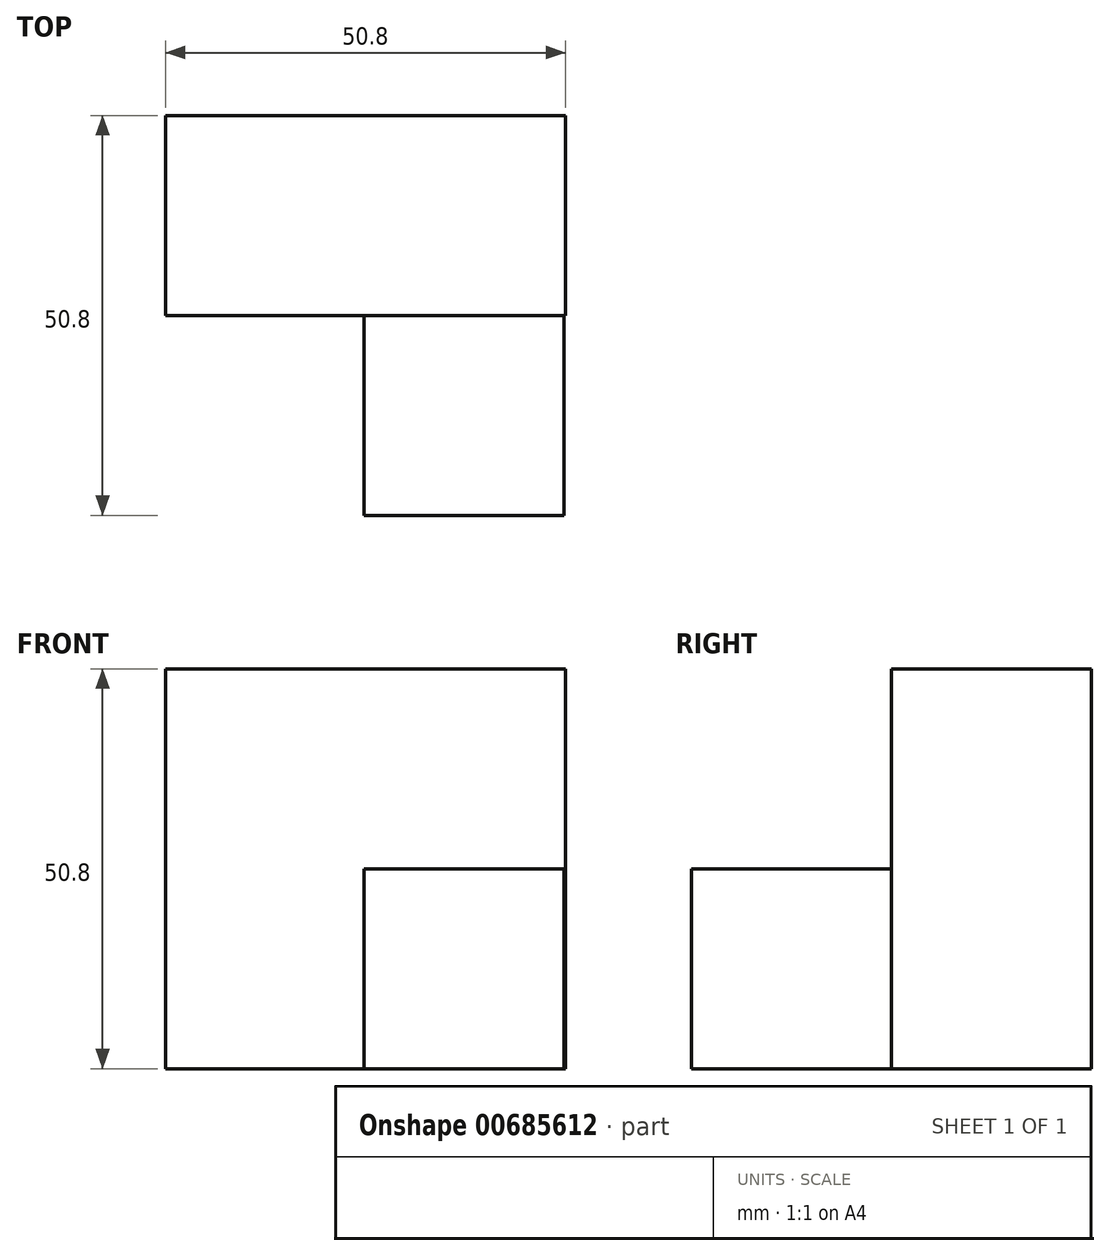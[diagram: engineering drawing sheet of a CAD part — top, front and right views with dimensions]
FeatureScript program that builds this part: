
annotation { "Feature Type Name" : "Feature", "Feature Type Description" : "" }
export const myFeature = defineFeature(function(context is Context, id is Id, definition is map)
    precondition{}
    {
        {
            var Q0;
            Q0=qCreatedBy(makeId("Front.planeOp"),FACE);
            var sketch = newSketch(context, id + "F0", { "sketchPlane" : qUnion([Q0])});
            skLineSegment(sketch, "E0.bottom", {"start": v(-31.04, 53.76) * mm, "end": v(19.76, 53.76) * mm});
            skLineSegment(sketch, "E0.top", {"start": v(-31.04, 2.96) * mm, "end": v(19.76, 2.96) * mm});
            skLineSegment(sketch, "E0.left", {"start": v(-31.04, 53.76) * mm, "end": v(-31.04, 2.96) * mm});
            skLineSegment(sketch, "E0.right", {"start": v(19.76, 53.76) * mm, "end": v(19.76, 2.96) * mm});
            skSolve(sketch);
        }
        {
            var Q0;
            Q0 = qSketchRegion(id + "F0", true);
            extrude(context, id + "F1", {"entities" : qUnion([Q0]), "depth" : 25.4 * mm, "offsetDistance" : 25.4 * mm});
        }
        {
            var Q0;
            Q0=qCreatedBy(makeId("Front.planeOp"),FACE);
            var sketch = newSketch(context, id + "F2", { "sketchPlane" : qUnion([Q0])});
            skLineSegment(sketch, "E1.bottom", {"start": v(19.58, 2.96) * mm, "end": v(-5.82, 2.96) * mm});
            skLineSegment(sketch, "E1.top", {"start": v(19.58, 28.36) * mm, "end": v(-5.82, 28.36) * mm});
            skLineSegment(sketch, "E1.left", {"start": v(19.58, 2.96) * mm, "end": v(19.58, 28.36) * mm});
            skLineSegment(sketch, "E1.right", {"start": v(-5.82, 2.96) * mm, "end": v(-5.82, 28.36) * mm});
            skSolve(sketch);
        }
        {
            var Q0;
            Q0 = qSketchRegion(id + "F2", true);
            extrude(context, id + "F3", {"entities" : qUnion([Q0]), "operationType" : NewBodyOperationType.ADD, "depth" : 50.8 * mm, "offsetDistance" : 25.4 * mm});
        }
    });
